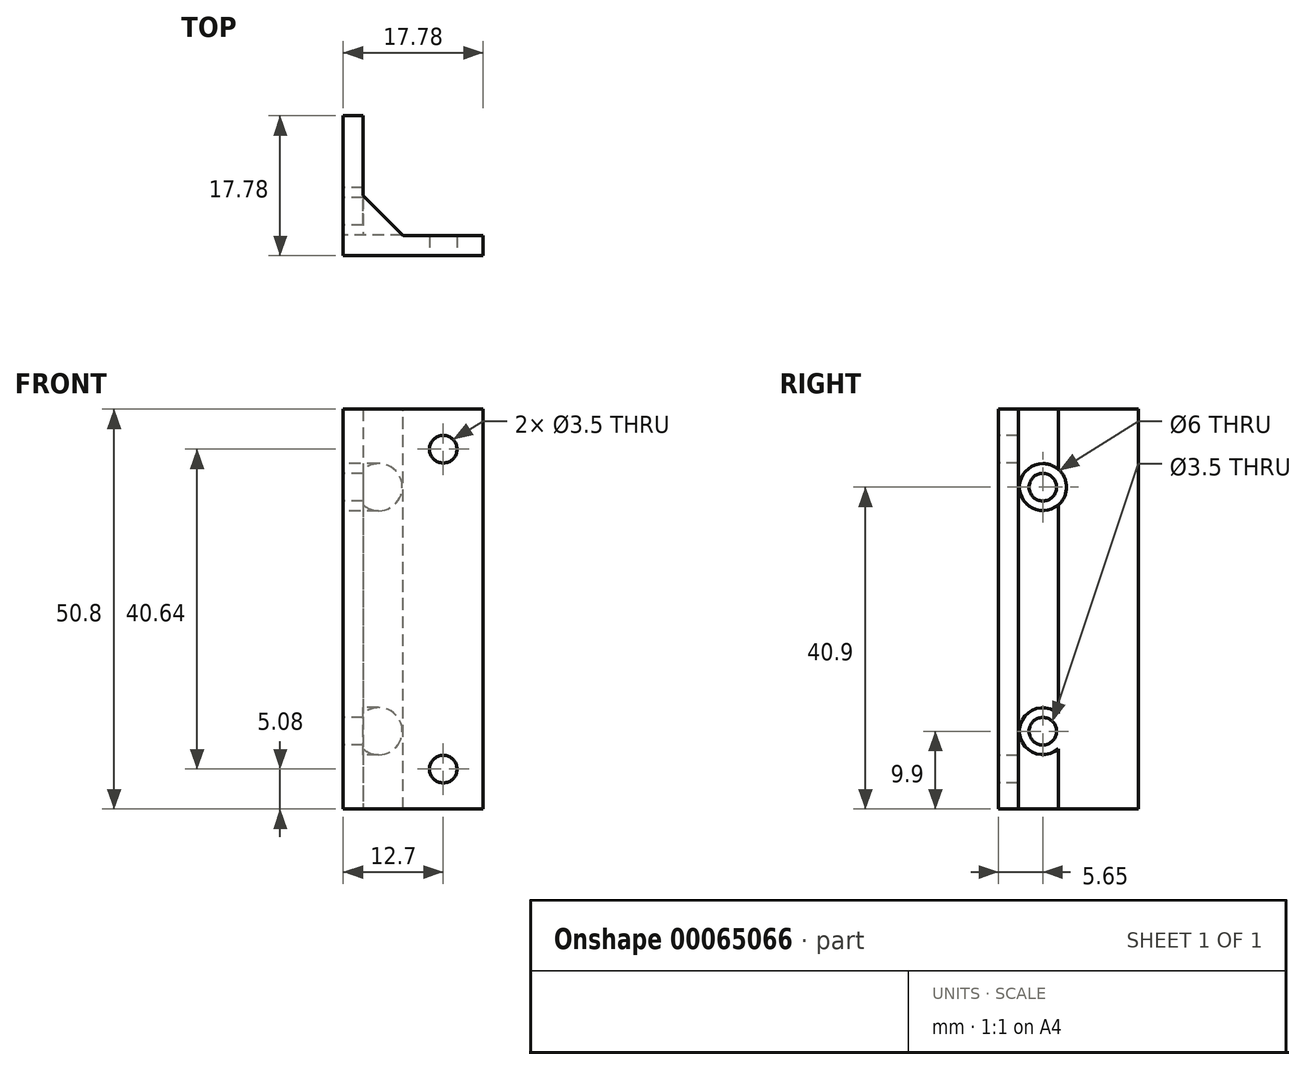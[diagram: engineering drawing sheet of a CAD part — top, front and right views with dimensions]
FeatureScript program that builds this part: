
annotation { "Feature Type Name" : "Feature", "Feature Type Description" : "" }
export const myFeature = defineFeature(function(context is Context, id is Id, definition is map)
    precondition{}
    {
        {
            var Q0;
            Q0=qCreatedBy(makeId("Top.planeOp"),FACE);
            var sketch = newSketch(context, id + "F0", { "sketchPlane" : qUnion([Q0])});
            skLineSegment(sketch, "E0.bottom", {"start": v(0, 0) * mm, "end": v(17.78, 0) * mm});
            skLineSegment(sketch, "E0.top", {"start": v(0, 17.78) * mm, "end": v(2.54, 17.78) * mm});
            skLineSegment(sketch, "E0.left", {"start": v(0, 0) * mm, "end": v(0, 17.78) * mm});
            skLineSegment(sketch, "E1.bottom", {"start": v(17.78, 0) * mm, "end": v(17.78, 0) * mm});
            skLineSegment(sketch, "E1.right", {"start": v(17.78, 0) * mm, "end": v(17.78, 2.54) * mm});
            skLineSegment(sketch, "E2.trimOffspring", {"start": v(2.54, 2.54) * mm, "end": v(2.54, 17.78) * mm});
            skLineSegment(sketch, "E3", {"start": v(2.54, 2.54) * mm, "end": v(17.78, 2.54) * mm});
            skSolve(sketch);
        }
        {
            var Q0;
            Q0 = qSketchRegion(id + "F0", true);
            var Q1;
            Q1=makeQuery(id+"F0.imprint","IMPRINT",FACE,{"disambiguationData":[TD([[makeQuery(id+"F0.imprint","IMPRINT",EDGE,{"derivedFrom":sQuery(id+"F0.wireOp",EDGE,"E0.bottom")}),1.0]])]});
            extrude(context, id + "F1", {"entities" : qUnion([Q0, Q1]), "depth" : 50.8 * mm, "offsetDistance" : 25.4 * mm});
        }
        {
            var Q0;
            Q0=makeQuery(id+"F1.opExtrude","SWEPT_FACE",FACE,{"disambiguationData":[OSD([sQuery(id+"F0.wireOp",EDGE,"E0.left")])]});
            var sketch = newSketch(context, id + "F2", { "sketchPlane" : qUnion([Q0])});
            skLineSegment(sketch, "E4", {"start": v(-5.65, 0) * mm, "end": v(-5.65, 50.8) * mm, "construction": true});
            skPoint(sketch, "E4.endSnap0", {"position": v(-8.9, 50.8) * mm});
            skLineSegment(sketch, "E5", {"start": v(-17.78, 25.4) * mm, "end": v(0, 25.4) * mm, "construction": true});
            skCircle(sketch, "E6", {"center": v(-5.65, 9.9) * mm, "radius": 1.75 * mm});
            skCircle(sketch, "E7.MirrorC", {"center": v(-5.65, 40.9) * mm, "radius": 1.75 * mm});
            skCircle(sketch, "E8", {"center": v(-5.65, 9.9) * mm, "radius": 3 * mm});
            skCircle(sketch, "E9.MirrorC", {"center": v(-5.65, 40.9) * mm, "radius": 3 * mm});
            skSolve(sketch);
        }
        {
            var Q0;
            Q0=makeQuery(id+"F2.imprint","IMPRINT",FACE,{"disambiguationData":[TD([[makeQuery(id+"F2.imprint","IMPRINT",EDGE,{"derivedFrom":sQuery(id+"F2.wireOp",EDGE,"E6")}),1.0]])]});
            var Q1;
            Q1=makeQuery(id+"F2.imprint","IMPRINT",FACE,{"disambiguationData":[TD([[makeQuery(id+"F2.imprint","IMPRINT",EDGE,{"derivedFrom":sQuery(id+"F2.wireOp",EDGE,"E7.MirrorC")}),-1.0]])]});
            extrude(context, id + "F3", {"entities" : qUnion([Q0, Q1]), "operationType" : NewBodyOperationType.REMOVE, "oppositeDirection" : true, "depth" : 25.4 * mm, "offsetDistance" : 25.4 * mm});
        }
        {
            var Q0;
            Q0=makeQuery(id+"F1.opExtrude","SWEPT_FACE",FACE,{"disambiguationData":[OSD([sQuery(id+"F0.wireOp",EDGE,"E0.bottom")])]});
            var sketch = newSketch(context, id + "F4", { "sketchPlane" : qUnion([Q0])});
            skLineSegment(sketch, "E10", {"start": v(17.78, 25.4) * mm, "end": v(0, 25.4) * mm, "construction": true});
            skCircle(sketch, "E11", {"center": v(12.7, 45.72) * mm, "radius": 1.75 * mm});
            skCircle(sketch, "E12.MirrorC", {"center": v(12.7, 5.08) * mm, "radius": 1.75 * mm});
            skSolve(sketch);
        }
        {
            var Q0;
            Q0=makeQuery(id+"F1.opExtrude","SWEPT_EDGE",EDGE,{"disambiguationData":[OSD([sQuery(id+"F0.wireOp",EDGE,"E2.trimOffspring"),sQuery(id+"F0.wireOp",EDGE,"E3")])]});
            chamfer(context, id + "F5", {"entities" : qUnion([Q0]), "width" : 5.08 * mm, "tangentPropagation" : true});
        }
        {
            var Q0;
            Q0=makeQuery(id+"F2.imprint","IMPRINT",FACE,{"disambiguationData":[TD([[makeQuery(id+"F2.imprint","IMPRINT",EDGE,{"derivedFrom":sQuery(id+"F2.wireOp",EDGE,"E7.MirrorC")}),1.0]])]});
            var Q1;
            Q1=makeQuery(id+"F2.imprint","IMPRINT",FACE,{"disambiguationData":[TD([[makeQuery(id+"F2.imprint","IMPRINT",EDGE,{"derivedFrom":sQuery(id+"F2.wireOp",EDGE,"E6")}),-1.0]])]});
            extrude(context, id + "F6", {"entities" : qUnion([Q0, Q1]), "operationType" : NewBodyOperationType.REMOVE, "endBound" : BoundingType.UP_TO_NEXT, "oppositeDirection" : true, "depth" : 9.4 * mm, "offsetDistance" : 25.4 * mm});
        }
        {
            var Q0;
            Q0=makeQuery(id+"F2.imprint","IMPRINT",FACE,{"disambiguationData":[TD([[makeQuery(id+"F2.imprint","IMPRINT",EDGE,{"derivedFrom":sQuery(id+"F2.wireOp",EDGE,"E7.MirrorC")}),1.0]])]});
            var Q1;
            Q1=makeQuery(id+"F2.imprint","IMPRINT",FACE,{"disambiguationData":[TD([[makeQuery(id+"F2.imprint","IMPRINT",EDGE,{"derivedFrom":sQuery(id+"F2.wireOp",EDGE,"E6")}),-1.0]])]});
            extrude(context, id + "F7", {"entities" : qUnion([Q0, Q1]), "operationType" : NewBodyOperationType.ADD, "oppositeDirection" : true, "depth" : 2.54 * mm, "offsetDistance" : 25.4 * mm});
        }
        {
            var Q0;
            Q0 = qSketchRegion(id + "F4", true);
            extrude(context, id + "F8", {"entities" : qUnion([Q0]), "operationType" : NewBodyOperationType.REMOVE, "endBound" : BoundingType.UP_TO_NEXT, "oppositeDirection" : true, "depth" : 25.4 * mm, "offsetDistance" : 25.4 * mm});
        }
    });
